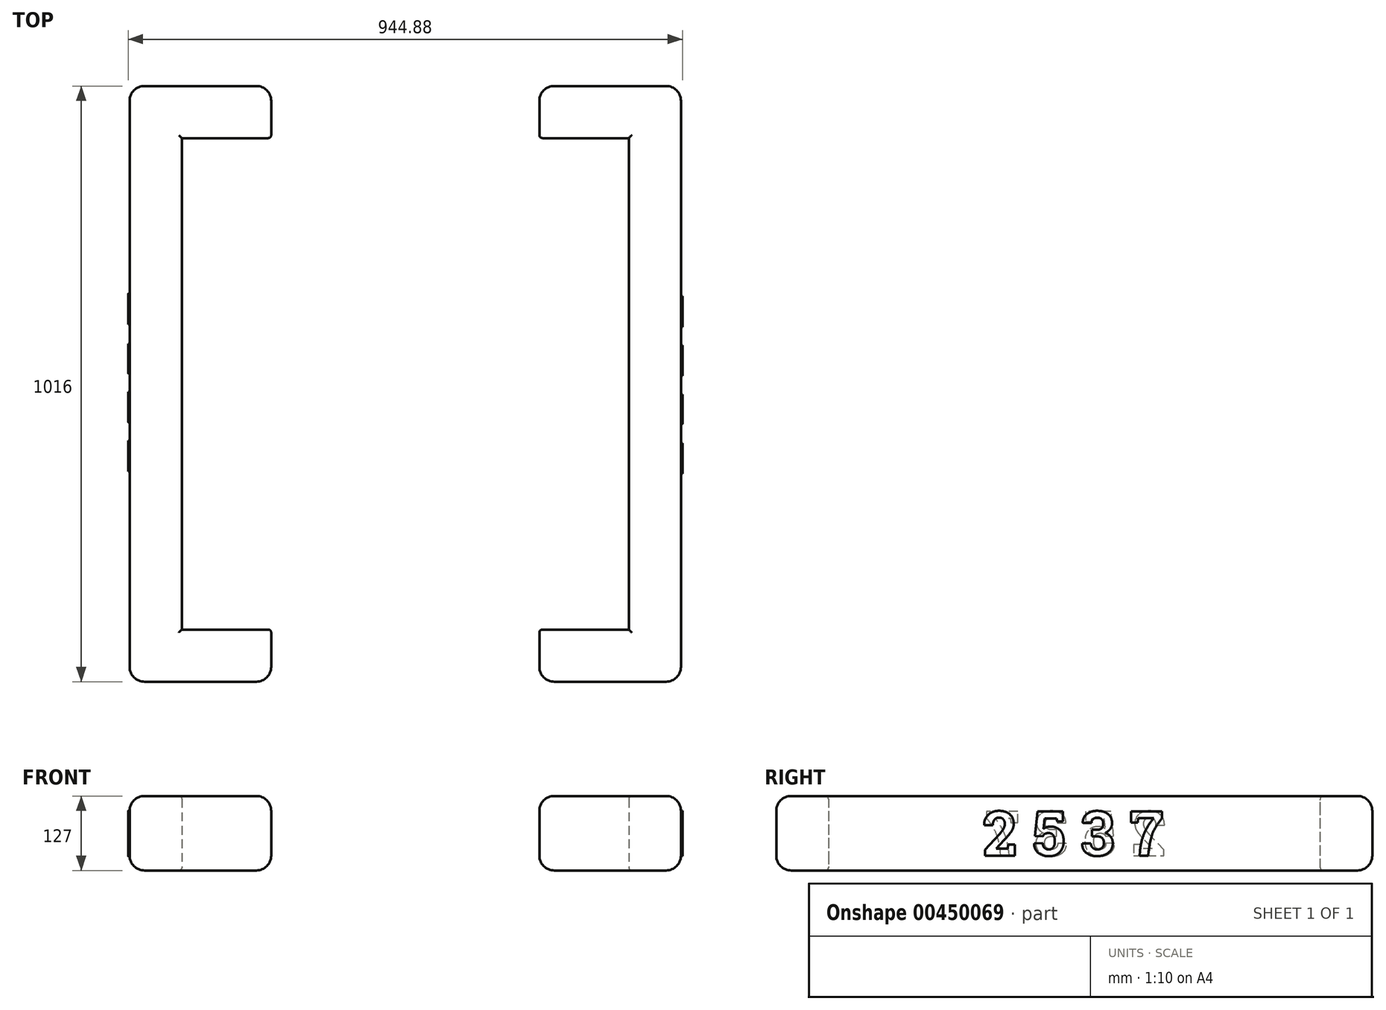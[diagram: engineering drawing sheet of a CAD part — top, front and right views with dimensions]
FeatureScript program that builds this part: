
annotation { "Feature Type Name" : "Feature", "Feature Type Description" : "" }
export const myFeature = defineFeature(function(context is Context, id is Id, definition is map)
    precondition{}
    {
        {
            var Q0;
            Q0=qCreatedBy(makeId("Right.planeOp"),FACE);
            var sketch = newSketch(context, id + "F0", { "sketchPlane" : qUnion([Q0])});
            skLineSegment(sketch, "E0.bottom", {"start": v(-508, 63.5) * mm, "end": v(508, 63.5) * mm});
            skLineSegment(sketch, "E0.top", {"start": v(-508, -63.5) * mm, "end": v(508, -63.5) * mm});
            skLineSegment(sketch, "E0.left", {"start": v(-508, 63.5) * mm, "end": v(-508, -63.5) * mm});
            skLineSegment(sketch, "E0.right", {"start": v(508, 63.5) * mm, "end": v(508, -63.5) * mm});
            skPoint(sketch, "E0.middle", {"position": v(0, 0) * mm});
            skSolve(sketch);
        }
        {
            var Q0;
            Q0=makeQuery(id+"F0.imprint","IMPRINT",FACE,{"disambiguationData":[TD([[makeQuery(id+"F0.imprint","IMPRINT",EDGE,{"derivedFrom":sQuery(id+"F0.wireOp",EDGE,"E0.bottom")}),-1.0]])]});
            extrude(context, id + "F1", {"entities" : qUnion([Q0]), "oppositeDirection" : true, "depth" : 88.9 * mm});
        }
        {
            var Q0;
            Q0=makeQuery(id+"F1.opExtrude","CAP_FACE",FACE,{"disambiguationData":[OSD([sQuery(id+"F0.wireOp",EDGE,"E0.bottom"),sQuery(id+"F0.wireOp",EDGE,"E0.top"),sQuery(id+"F0.wireOp",EDGE,"E0.left"),sQuery(id+"F0.wireOp",EDGE,"E0.right")])],"isStart":true});
            var sketch = newSketch(context, id + "F2", { "sketchPlane" : qUnion([Q0])});
            skLineSegment(sketch, "E1.bottom", {"start": v(-508, 63.5) * mm, "end": v(-419.1, 63.5) * mm});
            skLineSegment(sketch, "E1.top", {"start": v(-508, -63.5) * mm, "end": v(-419.1, -63.5) * mm});
            skLineSegment(sketch, "E1.left", {"start": v(-508, 63.5) * mm, "end": v(-508, -63.5) * mm});
            skLineSegment(sketch, "E1.right", {"start": v(-419.1, 63.5) * mm, "end": v(-419.1, -63.5) * mm});
            skLineSegment(sketch, "E2.bottom", {"start": v(508, -63.5) * mm, "end": v(419.1, -63.5) * mm});
            skLineSegment(sketch, "E2.top", {"start": v(508, 63.5) * mm, "end": v(419.1, 63.5) * mm});
            skLineSegment(sketch, "E2.left", {"start": v(508, -63.5) * mm, "end": v(508, 63.5) * mm});
            skLineSegment(sketch, "E2.right", {"start": v(419.1, -63.5) * mm, "end": v(419.1, 63.5) * mm});
            skSolve(sketch);
        }
        {
            var Q0;
            Q0=makeQuery(id+"F2.imprint","IMPRINT",FACE,{"disambiguationData":[TD([[makeQuery(id+"F2.imprint","IMPRINT",EDGE,{"derivedFrom":sQuery(id+"F2.wireOp",EDGE,"E2.bottom")}),1.0]])]});
            extrude(context, id + "F3", {"entities" : qUnion([Q0]), "operationType" : NewBodyOperationType.ADD, "depth" : 152.4 * mm, "offsetDistance" : 25.4 * mm});
        }
        {
            var Q0;
            Q0=makeQuery(id+"F2.imprint","IMPRINT",FACE,{"disambiguationData":[TD([[makeQuery(id+"F2.imprint","IMPRINT",EDGE,{"derivedFrom":sQuery(id+"F2.wireOp",EDGE,"E1.bottom")}),-1.0]])]});
            extrude(context, id + "F4", {"entities" : qUnion([Q0]), "operationType" : NewBodyOperationType.ADD, "depth" : 152.4 * mm, "offsetDistance" : 25.4 * mm});
        }
        {
            var Q0;
            Q0=makeQuery(id+"F1.opExtrude","CAP_EDGE",EDGE,{"disambiguationData":[OSD([sQuery(id+"F0.wireOp",EDGE,"E0.bottom")])],"isStart":false});
            var Q1;
            Q1=makeQuery(id+"F4.boolean.opBoolean","MERGE",EDGE,{"derivedFrom":[makeQuery(id+"F1.opExtrude","SWEPT_EDGE",EDGE,{"disambiguationData":[OSD([sQuery(id+"F0.wireOp",EDGE,"E0.bottom"),sQuery(id+"F0.wireOp",EDGE,"E0.left")])]}),makeQuery(id+"F4.opExtrude","SWEPT_EDGE",EDGE,{"disambiguationData":[OSD([sQuery(id+"F2.wireOp",EDGE,"E1.bottom"),sQuery(id+"F2.wireOp",EDGE,"E1.left")])]})]});
            var Q2;
            Q2=makeQuery(id+"F4.boolean.opBoolean","MERGE",EDGE,{"derivedFrom":[makeQuery(id+"F1.opExtrude","SWEPT_EDGE",EDGE,{"disambiguationData":[OSD([sQuery(id+"F0.wireOp",EDGE,"E0.bottom"),sQuery(id+"F0.wireOp",EDGE,"E0.right")])]}),makeQuery(id+"F4.opExtrude","SWEPT_EDGE",EDGE,{"disambiguationData":[OSD([sQuery(id+"F2.wireOp",EDGE,"E2.top"),sQuery(id+"F2.wireOp",EDGE,"E2.left")])]})]});
            var Q3;
            Q3=makeQuery(id+"F4.opExtrude","CAP_EDGE",EDGE,{"disambiguationData":[OSD([sQuery(id+"F2.wireOp",EDGE,"E1.bottom")])],"isStart":false});
            var Q4;
            Q4=makeQuery(id+"F4.opExtrude","CAP_EDGE",EDGE,{"disambiguationData":[OSD([sQuery(id+"F2.wireOp",EDGE,"E1.top")])],"isStart":false});
            var Q5;
            Q5=makeQuery(id+"F4.opExtrude","CAP_EDGE",EDGE,{"disambiguationData":[OSD([sQuery(id+"F2.wireOp",EDGE,"E1.left")])],"isStart":false});
            var Q6;
            Q6=makeQuery(id+"F4.boolean.opBoolean","MERGE",EDGE,{"derivedFrom":[makeQuery(id+"F1.opExtrude","SWEPT_EDGE",EDGE,{"disambiguationData":[OSD([sQuery(id+"F0.wireOp",EDGE,"E0.top"),sQuery(id+"F0.wireOp",EDGE,"E0.left")])]}),makeQuery(id+"F4.opExtrude","SWEPT_EDGE",EDGE,{"disambiguationData":[OSD([sQuery(id+"F2.wireOp",EDGE,"E1.top"),sQuery(id+"F2.wireOp",EDGE,"E1.left")])]})]});
            var Q7;
            Q7=makeQuery(id+"F1.opExtrude","CAP_EDGE",EDGE,{"disambiguationData":[OSD([sQuery(id+"F0.wireOp",EDGE,"E0.left")])],"isStart":false});
            var Q8;
            Q8=makeQuery(id+"F4.opExtrude","CAP_EDGE",EDGE,{"disambiguationData":[OSD([sQuery(id+"F2.wireOp",EDGE,"E2.top")])],"isStart":false});
            var Q9;
            Q9=makeQuery(id+"F4.opExtrude","CAP_EDGE",EDGE,{"disambiguationData":[OSD([sQuery(id+"F2.wireOp",EDGE,"E2.bottom")])],"isStart":false});
            var Q10;
            Q10=makeQuery(id+"F4.opExtrude","CAP_EDGE",EDGE,{"disambiguationData":[OSD([sQuery(id+"F2.wireOp",EDGE,"E2.left")])],"isStart":false});
            var Q11;
            Q11=makeQuery(id+"F4.boolean.opBoolean","MERGE",EDGE,{"derivedFrom":[makeQuery(id+"F1.opExtrude","SWEPT_EDGE",EDGE,{"disambiguationData":[OSD([sQuery(id+"F0.wireOp",EDGE,"E0.top"),sQuery(id+"F0.wireOp",EDGE,"E0.right")])]}),makeQuery(id+"F4.opExtrude","SWEPT_EDGE",EDGE,{"disambiguationData":[OSD([sQuery(id+"F2.wireOp",EDGE,"E2.bottom"),sQuery(id+"F2.wireOp",EDGE,"E2.left")])]})]});
            var Q12;
            Q12=makeQuery(id+"F1.opExtrude","CAP_EDGE",EDGE,{"disambiguationData":[OSD([sQuery(id+"F0.wireOp",EDGE,"E0.right")])],"isStart":false});
            var Q13;
            Q13=makeQuery(id+"F1.opExtrude","CAP_EDGE",EDGE,{"disambiguationData":[OSD([sQuery(id+"F0.wireOp",EDGE,"E0.top")])],"isStart":false});
            var Q14;
            Q14=makeQuery(id+"F3.boolean.opBoolean","MERGE",EDGE,{"derivedFrom":[makeQuery(id+"F1.opExtrude","SWEPT_EDGE",EDGE,{"disambiguationData":[OSD([sQuery(id+"F0.wireOp",EDGE,"E0.bottom"),sQuery(id+"F0.wireOp",EDGE,"E0.right")])]}),makeQuery(id+"F3.opExtrude","SWEPT_EDGE",EDGE,{"disambiguationData":[OSD([sQuery(id+"F2.wireOp",EDGE,"E2.top"),sQuery(id+"F2.wireOp",EDGE,"E2.left")])]})]});
            var Q15;
            Q15=makeQuery(id+"F3.opExtrude","CAP_EDGE",EDGE,{"disambiguationData":[OSD([sQuery(id+"F2.wireOp",EDGE,"E2.top")])],"isStart":false});
            var Q16;
            Q16=makeQuery(id+"F3.boolean.opBoolean","MERGE",EDGE,{"derivedFrom":[makeQuery(id+"F1.opExtrude","SWEPT_EDGE",EDGE,{"disambiguationData":[OSD([sQuery(id+"F0.wireOp",EDGE,"E0.top"),sQuery(id+"F0.wireOp",EDGE,"E0.right")])]}),makeQuery(id+"F3.opExtrude","SWEPT_EDGE",EDGE,{"disambiguationData":[OSD([sQuery(id+"F2.wireOp",EDGE,"E2.bottom"),sQuery(id+"F2.wireOp",EDGE,"E2.left")])]})]});
            var Q17;
            Q17=makeQuery(id+"F3.opExtrude","CAP_EDGE",EDGE,{"disambiguationData":[OSD([sQuery(id+"F2.wireOp",EDGE,"E2.left")])],"isStart":false});
            var Q18;
            Q18=makeQuery(id+"F3.opExtrude","CAP_EDGE",EDGE,{"disambiguationData":[OSD([sQuery(id+"F2.wireOp",EDGE,"E2.bottom")])],"isStart":false});
            fillet(context, id + "F5", {"entities" : qUnion([Q0, Q1, Q2, Q3, Q4, Q5, Q6, Q7, Q8, Q9, Q10, Q11, Q12, Q13, Q14, Q15, Q16, Q17, Q18]), "radius" : 25.4 * mm, "tangentPropagation" : true, "allowEdgeOverflow" : false});
        }
        {
            var Q0;
            Q0=makeQuery(id+"F1.opExtrude","CAP_EDGE",EDGE,{"disambiguationData":[OSD([sQuery(id+"F0.wireOp",EDGE,"E0.bottom")])],"isStart":true});
            var Q1;
            Q1=makeQuery(id+"F3.opExtrude","SWEPT_EDGE",EDGE,{"disambiguationData":[OSD([sQuery(id+"F0.wireOp",EDGE,"E0.bottom"),sQuery(id+"F2.wireOp",EDGE,"E2.top"),sQuery(id+"F2.wireOp",EDGE,"E2.right")])]});
            var Q2;
            Q2=makeQuery(id+"F3.opExtrude","SWEPT_EDGE",EDGE,{"disambiguationData":[OSD([sQuery(id+"F0.wireOp",EDGE,"E0.top"),sQuery(id+"F2.wireOp",EDGE,"E2.bottom"),sQuery(id+"F2.wireOp",EDGE,"E2.right")])]});
            var Q3;
            Q3=makeQuery(id+"F1.opExtrude","CAP_EDGE",EDGE,{"disambiguationData":[OSD([sQuery(id+"F0.wireOp",EDGE,"E0.top")])],"isStart":true});
            var Q4;
            Q4=makeQuery(id+"F3.opExtrude","CAP_EDGE",EDGE,{"disambiguationData":[OSD([sQuery(id+"F2.wireOp",EDGE,"E2.right")])],"isStart":true});
            var Q5;
            Q5=makeQuery(id+"F4.opExtrude","SWEPT_EDGE",EDGE,{"disambiguationData":[OSD([sQuery(id+"F0.wireOp",EDGE,"E0.bottom"),sQuery(id+"F2.wireOp",EDGE,"E1.bottom"),sQuery(id+"F2.wireOp",EDGE,"E1.right")])]});
            var Q6;
            Q6=makeQuery(id+"F4.opExtrude","CAP_EDGE",EDGE,{"disambiguationData":[OSD([sQuery(id+"F2.wireOp",EDGE,"E1.right")])],"isStart":true});
            fillet(context, id + "F6", {"entities" : qUnion([Q0, Q1, Q2, Q3, Q4, Q5, Q6]), "radius" : 5.08 * mm, "tangentPropagation" : true, "allowEdgeOverflow" : false});
        }
        {
            var Q0;
            Q0=makeQuery(id+"F1.opExtrude","SWEPT_BODY",BODY,{"disambiguationData":[OSD([sQuery(id+"F0.wireOp",EDGE,"E0.bottom"),sQuery(id+"F0.wireOp",EDGE,"E0.top"),sQuery(id+"F0.wireOp",EDGE,"E0.left"),sQuery(id+"F0.wireOp",EDGE,"E0.right")])]});
            transform(context, id + "F7", {"entities" : qUnion([Q0]), "transformType" : TransformType.TRANSLATION_3D, "dx" : -381 * mm, "dy" : 0 * mm, "dz" : 0 * mm, "makeCopy" : false});
        }
        {
            var Q0;
            Q0=makeQuery(id+"F1.opExtrude","SWEPT_BODY",BODY,{"disambiguationData":[OSD([sQuery(id+"F0.wireOp",EDGE,"E0.bottom"),sQuery(id+"F0.wireOp",EDGE,"E0.top"),sQuery(id+"F0.wireOp",EDGE,"E0.left"),sQuery(id+"F0.wireOp",EDGE,"E0.right")])]});
            var Q1;
            Q1=qCreatedBy(makeId("Right.planeOp"),FACE);
            mirror(context, id + "F8", {"entities" : qUnion([Q0]), "mirrorPlane" : qUnion([Q1])});
        }
        {
            var Q0;
            Q0=makeQuery(id+"F1.opExtrude","CAP_FACE",FACE,{"disambiguationData":[OSD([sQuery(id+"F0.wireOp",EDGE,"E0.bottom"),sQuery(id+"F0.wireOp",EDGE,"E0.top"),sQuery(id+"F0.wireOp",EDGE,"E0.left"),sQuery(id+"F0.wireOp",EDGE,"E0.right")])],"isStart":false});
            var sketch = newSketch(context, id + "F9", { "sketchPlane" : qUnion([Q0])});
            skText(sketch, "E3", { "text": "2 5 3 7", "fontName": "RobotoSlab-Bold.ttf"});
            const initialGuessF9  = {"E3": [-0.15622, -0.0381, 1, 0, 0.0762]};
            skSetInitialGuess(sketch, initialGuessF9);
            skSolve(sketch);
        }
        {
            var Q0;
            Q0 = qSketchRegion(id + "F9", true);
            extrude(context, id + "F10", {"entities" : qUnion([Q0]), "operationType" : NewBodyOperationType.ADD, "depth" : 2.54 * mm});
        }
        {
            var Q0;
            Q0=makeQuery(id+"F8.opPattern","COPY",FACE,{"derivedFrom":makeQuery(id+"F1.opExtrude","CAP_FACE",FACE,{"disambiguationData":[OSD([sQuery(id+"F0.wireOp",EDGE,"E0.bottom"),sQuery(id+"F0.wireOp",EDGE,"E0.top"),sQuery(id+"F0.wireOp",EDGE,"E0.left"),sQuery(id+"F0.wireOp",EDGE,"E0.right")])],"isStart":false}),"instanceName":"1"});
            var sketch = newSketch(context, id + "F11", { "sketchPlane" : qUnion([Q0])});
            skText(sketch, "E4", { "text": "2 5 3 7", "fontName": "RobotoSlab-Bold.ttf"});
            const initialGuessF11  = {"E4": [-0.15622, -0.0381, 1, 0, 0.0762]};
            skSetInitialGuess(sketch, initialGuessF11);
            skSolve(sketch);
        }
        {
            var Q0;
            Q0 = qSketchRegion(id + "F11", true);
            extrude(context, id + "F12", {"entities" : qUnion([Q0]), "operationType" : NewBodyOperationType.ADD, "depth" : 2.54 * mm});
        }
    });
